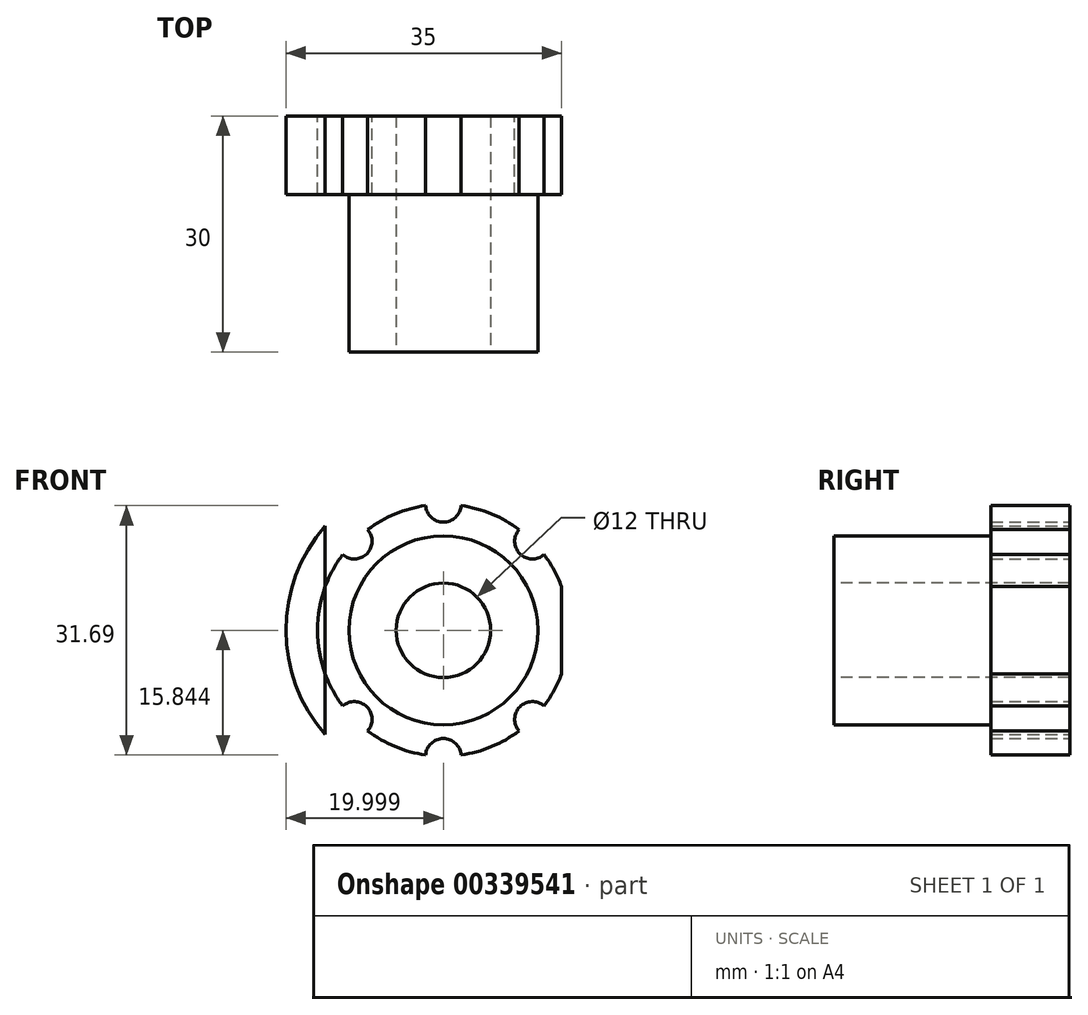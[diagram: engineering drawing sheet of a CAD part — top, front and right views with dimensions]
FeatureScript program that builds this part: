
annotation { "Feature Type Name" : "Feature", "Feature Type Description" : "" }
export const myFeature = defineFeature(function(context is Context, id is Id, definition is map)
    precondition{}
    {
        {
            var Q0;
            Q0=qCreatedBy(makeId("Front.planeOp"),FACE);
            var sketch = newSketch(context, id + "F0", { "sketchPlane" : qUnion([Q0])});
            skCircle(sketch, "E0", {"center": v(-5.33, 2.27) * mm, "radius": 20 * mm});
            skCircle(sketch, "E1", {"center": v(-5.33, 2.27) * mm, "radius": 12 * mm});
            skCircle(sketch, "E2", {"center": v(-5.33, 2.27) * mm, "radius": 16 * mm});
            skCircle(sketch, "E3", {"center": v(-16.64, -9.04) * mm, "radius": 2.25 * mm});
            skCircle(sketch, "E4", {"center": v(5.98, -9.04) * mm, "radius": 2.25 * mm});
            skCircle(sketch, "E5", {"center": v(-16.64, 13.59) * mm, "radius": 2.25 * mm});
            skCircle(sketch, "E6", {"center": v(5.98, 13.59) * mm, "radius": 2.25 * mm});
            skLineSegment(sketch, "E7", {"start": v(-5.33, 2.27) * mm, "end": v(-34, 30.95) * mm, "construction": true});
            skLineSegment(sketch, "E8", {"start": v(-5.33, 2.27) * mm, "end": v(23.88, 31.49) * mm, "construction": true});
            skLineSegment(sketch, "E9", {"start": v(-5.33, 2.27) * mm, "end": v(-29.07, -21.47) * mm, "construction": true});
            skLineSegment(sketch, "E10", {"start": v(-5.33, 2.27) * mm, "end": v(20.22, -23.28) * mm, "construction": true});
            skLineSegment(sketch, "E11", {"start": v(9.67, 26.4) * mm, "end": v(9.67, -34.45) * mm});
            skLineSegment(sketch, "E12", {"start": v(-20.33, 22.84) * mm, "end": v(-20.33, -22.26) * mm});
            skLineSegment(sketch, "E13", {"start": v(-5.33, 2.27) * mm, "end": v(-5.33, -27.93) * mm, "construction": true});
            skLineSegment(sketch, "E14", {"start": v(-5.33, 2.27) * mm, "end": v(-5.33, 35.21) * mm, "construction": true});
            skCircle(sketch, "E15", {"center": v(-5.33, -13.73) * mm, "radius": 2.25 * mm});
            skCircle(sketch, "E16", {"center": v(-5.33, 18.27) * mm, "radius": 2.25 * mm});
            skSolve(sketch);
        }
        {
            var Q0;
            Q0=makeQuery(id+"F0.imprint","IMPRINT",FACE,{"disambiguationData":[TD([[makeQuery(id+"F0.imprint","IMPRINT",EDGE,{"derivedFrom":sQuery(id+"F0.wireOp",EDGE,"E1")}),-1.0]])]});
            var Q1;
            {var subQ11=sQuery(id+"F0.wireOp",EDGE,"E12");var subQ12=sQuery(id+"F0.wireOp",EDGE,"E0");var subQ13=makeQuery(id+"F0.imprint","INTERSECT",VERTEX,{"disambiguationData":[OD(0.0)],"derivedFrom":[subQ12,subQ11]});Q1=makeQuery(id+"F0.imprint","IMPRINT",FACE,{"disambiguationData":[TD([[makeQuery(id+"F0.imprint","IMPRINT",EDGE,{"disambiguationData":[TD([[subQ13,1.0]])],"derivedFrom":subQ12}),1.0]])]});}
            var Q2;
            {var subQ8=sQuery(id+"F0.wireOp",EDGE,"E12");var subQ11=sQuery(id+"F0.wireOp",EDGE,"E0");var subQ12=makeQuery(id+"F0.imprint","INTERSECT",VERTEX,{"disambiguationData":[OD(1.0)],"derivedFrom":[subQ11,subQ8]});Q2=makeQuery(id+"F0.imprint","IMPRINT",FACE,{"disambiguationData":[TD([[makeQuery(id+"F0.imprint","IMPRINT",EDGE,{"disambiguationData":[TD([[subQ12,-1.0]])],"derivedFrom":subQ11}),1.0]])]});}
            var Q3;
            Q3=makeQuery(id+"F0.imprint","IMPRINT",FACE,{"disambiguationData":[TD([[makeQuery(id+"F0.imprint","IMPRINT",EDGE,{"derivedFrom":sQuery(id+"F0.wireOp",EDGE,"E1")}),1.0]])]});
            extrude(context, id + "F1", {"entities" : qUnion([Q0, Q1, Q2, Q3]), "depth" : 10 * mm});
        }
        {
            var Q0;
            Q0=makeQuery(id+"F0.imprint","IMPRINT",FACE,{"disambiguationData":[TD([[makeQuery(id+"F0.imprint","IMPRINT",EDGE,{"derivedFrom":sQuery(id+"F0.wireOp",EDGE,"E1")}),1.0]])]});
            extrude(context, id + "F2", {"entities" : qUnion([Q0]), "operationType" : NewBodyOperationType.ADD, "depth" : 30 * mm});
        }
        {
            var Q0;
            Q0=sQuery(id+"F0.wireOp",VERTEX,"E13.start");
            var Q1;
            Q1=makeQuery(id+"F1.opExtrude","SWEPT_BODY",BODY,{"disambiguationData":[OSD([sQuery(id+"F0.wireOp",EDGE,"E0"),sQuery(id+"F0.wireOp",EDGE,"E3"),sQuery(id+"F0.wireOp",EDGE,"E4"),sQuery(id+"F0.wireOp",EDGE,"E5"),sQuery(id+"F0.wireOp",EDGE,"E6"),sQuery(id+"F0.wireOp",EDGE,"E11"),sQuery(id+"F0.wireOp",EDGE,"E12"),sQuery(id+"F0.wireOp",EDGE,"E15"),sQuery(id+"F0.wireOp",EDGE,"E16")])]});
            hole(context, id + "F3", {"style" : HoleStyle.SIMPLE, "endStyle" : HoleEndStyle.BLIND, "oppositeDirection" : true, "holeDiameter" : 12 * mm, "holeDepth" : 50 * mm, "isTappedThrough" : true, "tappedDepth" : 12 * mm, "tapClearance" : 3, "locations" : qUnion([Q0]), "scope" : qUnion([Q1])});
        }
    });
